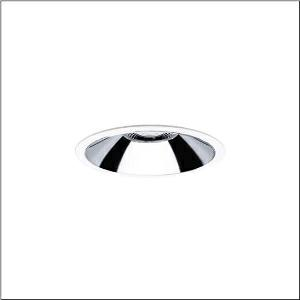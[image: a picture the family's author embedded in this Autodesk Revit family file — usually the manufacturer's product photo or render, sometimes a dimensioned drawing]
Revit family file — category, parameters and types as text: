
# Revit family: lunis_21_xl_51db15mf3d
name_source: partatom
category: Lighting Fixtures
units: mm (PartAtom-declared; Revit-internal decimal feet)

## family parameters
Cut with Voids When Loaded = No
Host = Face
Light Source = No
Part Type = Normal
Room Calculation Point = No
Round Connector Dimension = Use Diameter
Shared = No

## types (1)
- --- (1 x LED, 2620 lm, 23.5 W, 3000K)
    Apparent Load = 24 VA
    CIE Flux Codes = 89 99 100 100 100
    Color Rendering = 80
    Color Temperature = 3000K
    Default Elevation = 1800 mm
    Description = Lunis 21,  XL, downlight, of PC, light emission: direct distribution, LED rated luminous flux: 2.180lm, light colour: 830, control gear: ECG, with terminal, 3-pole, mains connection: 220..240V, AC, housing, round, of diecast aluminium, traffic white (RAL 9016), diameter: 213mm, protection rating (complete): IP20, protection rating (on room side): IP54, insulation class (complete): insulation class II (safety insulation), certification: CE, impact resistance: IK02, packaging unit: 1 piece
    Height = 0 mm  [stored 0 ft]
    Lamp = 1 x LED
    Lamp Light Flux = 2620 lm
    Lamp Power = 23.5 W
    Lamp count = 1
    Length = 213 mm
    Luminous efficacy = 111 lm/W
    Manufacturer = Siteco
    ModVariant = No
    Model = 51DB15MF3D
    Mounting Place = Ceiling
    Mounting Type = Recessed
    Number of Poles = 1
    OnlyDefault = Yes
    Power Factor = 1
    Product Name = Lunis 21 XL
    Product group = downlight
    ProductGroupID = 400
    Protection Class = Protection class II
    Protection Degree = IP 20
    RLX_Detail_Level = 1
    RLX_Emergency_Light_Flux = 0 lm
    RLX_Emergency_Type = 0
    RLX_Emergency_Type_DB = No
    RlxData = <blob elided: 27637 chars, md5=d78677e8>
    Socket = socket
    Standby Power = 0 W
    System Light Flux = 2620 lm
    System Power = 24 W
    Type Comments = factory setting: luminous flux: 100 % | (ON | ON)
    Type Image = l_1287385.jpg
    URL = http://relux.com
    VarID = @adj_083059
    Voltage = 0 V
    Weight = 0.00 kg
    Width = 0 mm  [stored 0 ft]

note: [stored X ft] marks values corroborated as IEEE doubles in the binary element streams (Revit-internal decimal feet)

## geometry (parser evidence)
native form markers: Blend x4, Sweep x12
no freeform markers — native parametric forms only
